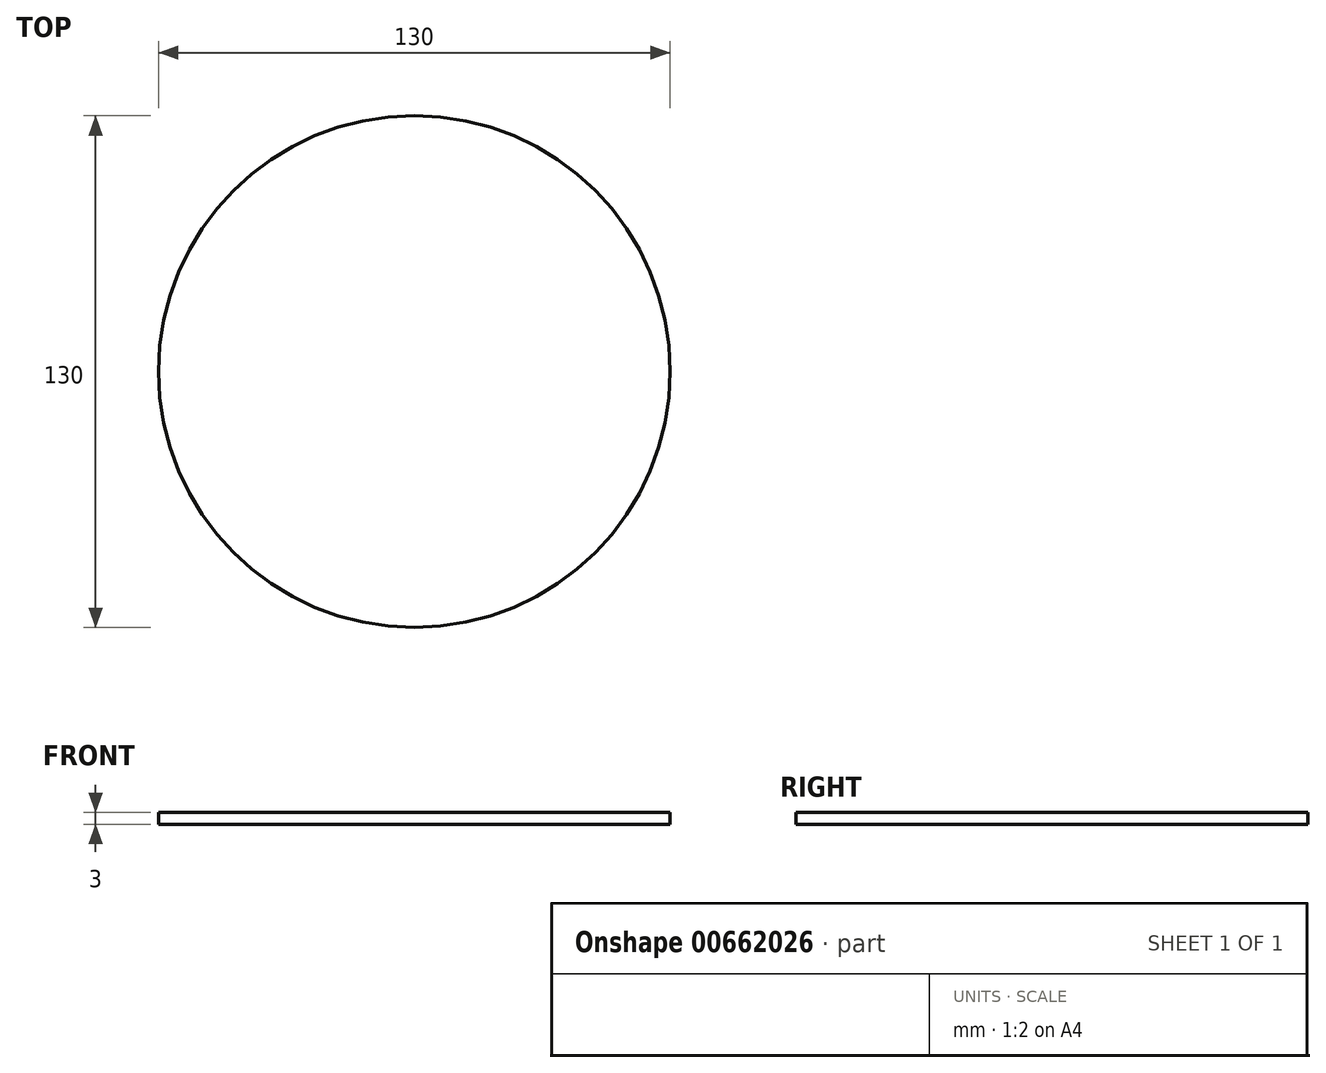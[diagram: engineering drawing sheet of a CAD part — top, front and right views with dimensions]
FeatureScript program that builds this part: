
annotation { "Feature Type Name" : "Feature", "Feature Type Description" : "" }
export const myFeature = defineFeature(function(context is Context, id is Id, definition is map)
    precondition{}
    {
        {
            var Q0;
            Q0=qCreatedBy(makeId("Top.planeOp"),FACE);
            var sketch = newSketch(context, id + "F0", { "sketchPlane" : qUnion([Q0])});
            skCircle(sketch, "E0", {"center": v(0, 0) * mm, "radius": 65 * mm});
            skSolve(sketch);
        }
        {
            var Q0;
            Q0 = qSketchRegion(id + "F0", true);
            extrude(context, id + "F1", {"entities" : qUnion([Q0]), "depth" : 3 * mm, "offsetDistance" : 25 * mm});
        }
    });
